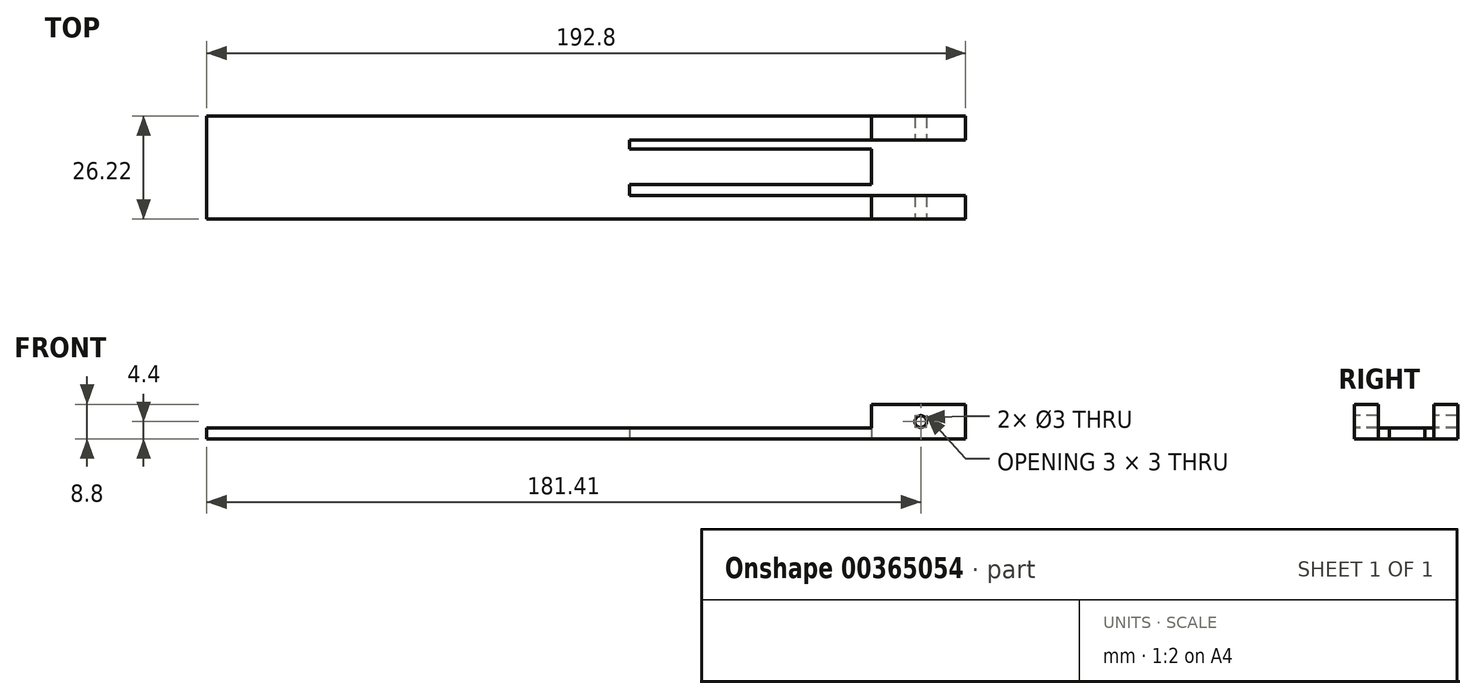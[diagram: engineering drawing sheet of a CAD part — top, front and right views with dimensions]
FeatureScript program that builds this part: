
annotation { "Feature Type Name" : "Feature", "Feature Type Description" : "" }
export const myFeature = defineFeature(function(context is Context, id is Id, definition is map)
    precondition{}
    {
        {
            var Q0;
            Q0=qCreatedBy(makeId("Top.planeOp"),FACE);
            var sketch = newSketch(context, id + "F0", { "sketchPlane" : qUnion([Q0])});
            skLineSegment(sketch, "E0.bottom", {"start": v(75, -12.39) * mm, "end": v(-75, -12.39) * mm});
            skLineSegment(sketch, "E0.top", {"start": v(75, 12.39) * mm, "end": v(-75, 12.39) * mm});
            skLineSegment(sketch, "E0.left", {"start": v(75, -12.39) * mm, "end": v(75, 12.39) * mm});
            skLineSegment(sketch, "E0.right", {"start": v(-75, -12.39) * mm, "end": v(-75, 12.39) * mm});
            skPoint(sketch, "E0.middle", {"position": v(0, 0) * mm});
            skLineSegment(sketch, "E1.bottom", {"start": v(-10.37, 7.78) * mm, "end": v(75, 7.78) * mm});
            skLineSegment(sketch, "E1.top", {"start": v(-10.37, 5.43) * mm, "end": v(75, 5.43) * mm});
            skLineSegment(sketch, "E1.left", {"start": v(-10.37, 7.78) * mm, "end": v(-10.37, 5.43) * mm});
            skLineSegment(sketch, "E2.bottom", {"start": v(-10.37, -3.6) * mm, "end": v(75, -3.6) * mm});
            skLineSegment(sketch, "E2.top", {"start": v(-10.37, -6.34) * mm, "end": v(75, -6.34) * mm});
            skLineSegment(sketch, "E2.left", {"start": v(-10.37, -3.6) * mm, "end": v(-10.37, -6.34) * mm});
            skLineSegment(sketch, "E2.right", {"start": v(75, -3.6) * mm, "end": v(75, -6.34) * mm});
            skSolve(sketch);
        }
        {
            var Q0;
            {var subQ5=sQuery(id+"F0.wireOp",EDGE,"E0.bottom");Q0=makeQuery(id+"F0.imprint","IMPRINT",FACE,{"disambiguationData":[TD([[makeQuery(id+"F0.imprint","IMPRINT",EDGE,{"derivedFrom":subQ5}),-1.0]])]});}
            extrude(context, id + "F1", {"entities" : qUnion([Q0]), "depth" : 2.8 * mm});
        }
        {
            var Q0;
            Q0=makeQuery(id+"F1.opExtrude","SWEPT_FACE",FACE,{"disambiguationData":[OSD([sQuery(id+"F0.wireOp",EDGE,"E0.right")])]});
            extrude(context, id + "F2", {"entities" : qUnion([Q0]), "operationType" : NewBodyOperationType.ADD, "depth" : 42.8 * mm});
        }
        {
            var Q0;
            {var subQ0=sQuery(id+"F0.wireOp",EDGE,"E0.top");Q0=makeQuery(id+"F2.boolean.opBoolean","MERGE",FACE,{"derivedFrom":[makeQuery(id+"F1.opExtrude","SWEPT_FACE",FACE,{"disambiguationData":[OSD([subQ0])]}),makeQuery(id+"F2.opExtrude","SWEPT_FACE",FACE,{"disambiguationData":[OSD([subQ0,sQuery(id+"F0.wireOp",EDGE,"E0.right")])]})]});}
            extrude(context, id + "F3", {"entities" : qUnion([Q0]), "operationType" : NewBodyOperationType.ADD, "depth" : 1.44 * mm});
        }
        {
            var Q0;
            Q0=makeQuery(id+"F3.opExtrude","CAP_FACE",FACE,{"disambiguationData":[OSD([sQuery(id+"F0.wireOp",EDGE,"E0.top"),sQuery(id+"F0.wireOp",EDGE,"E0.right")])],"isStart":false});
            extrude(context, id + "F4", {"entities" : qUnion([Q0]), "operationType" : NewBodyOperationType.REMOVE, "depth" : 85.38 * mm});
        }
        {
            var Q0;
            {var subQ0=sQuery(id+"F0.wireOp",EDGE,"E0.right");var subQ1=sQuery(id+"F0.wireOp",EDGE,"E0.top");Q0=makeQuery(id+"F3.boolean.opBoolean","MERGE",FACE,{"derivedFrom":[makeQuery(id+"F2.boolean.opBoolean","MERGE",FACE,{"derivedFrom":[makeQuery(id+"F1.opExtrude","CAP_FACE",FACE,{"disambiguationData":[OSD([sQuery(id+"F0.wireOp",EDGE,"E0.bottom"),subQ1,sQuery(id+"F0.wireOp",EDGE,"E0.left"),subQ0,sQuery(id+"F0.wireOp",EDGE,"E1.bottom"),sQuery(id+"F0.wireOp",EDGE,"E1.top"),sQuery(id+"F0.wireOp",EDGE,"E1.left"),sQuery(id+"F0.wireOp",EDGE,"E2.bottom"),sQuery(id+"F0.wireOp",EDGE,"E2.top"),sQuery(id+"F0.wireOp",EDGE,"E2.left")])],"isStart":false}),makeQuery(id+"F2.opExtrude","SWEPT_FACE",FACE,{"disambiguationData":[OSD([subQ0]),TDD([makeQuery(id+"F1.opExtrude","CAP_EDGE",EDGE,{"disambiguationData":[OSD([subQ0])],"isStart":false})])]})]}),makeQuery(id+"F3.opExtrude","SWEPT_FACE",FACE,{"disambiguationData":[OSD([subQ1,subQ0]),TDD([makeQuery(id+"F2.boolean.opBoolean","MERGE",EDGE,{"derivedFrom":[makeQuery(id+"F1.opExtrude","CAP_EDGE",EDGE,{"disambiguationData":[OSD([subQ1])],"isStart":false}),makeQuery(id+"F2.opExtrude","SWEPT_EDGE",EDGE,{"disambiguationData":[OSD([subQ1,subQ0]),TDD([makeQuery(id+"F1.opExtrude","CAP_VERTEX",VERTEX,{"disambiguationData":[OSD([subQ1,subQ0])],"isStart":false})])]})]})])]})]});}
            var sketch = newSketch(context, id + "F5", { "sketchPlane" : qUnion([Q0])});
            skLineSegment(sketch, "E3", {"start": v(51.11, 13.83) * mm, "end": v(51.11, 7.78) * mm});
            skLineSegment(sketch, "E4", {"start": v(51.11, -6.34) * mm, "end": v(51.11, -12.39) * mm});
            skSolve(sketch);
        }
        {
            var Q0;
            {var subQ0=sQuery(id+"F5.wireOp",EDGE,"E3");Q0=makeQuery(id+"F5.imprint","IMPRINT",FACE,{"disambiguationData":[TD([[makeQuery(id+"F5.imprint","IMPRINT",EDGE,{"derivedFrom":subQ0}),1.0]])]});}
            var Q1;
            {var subQ0=sQuery(id+"F5.wireOp",EDGE,"E4");Q1=makeQuery(id+"F5.imprint","IMPRINT",FACE,{"disambiguationData":[TD([[makeQuery(id+"F5.imprint","IMPRINT",EDGE,{"derivedFrom":subQ0}),1.0]])]});}
            extrude(context, id + "F6", {"entities" : qUnion([Q0, Q1]), "operationType" : NewBodyOperationType.ADD, "depth" : 6 * mm});
        }
        {
            var Q0;
            {var subQ0=sQuery(id+"F0.wireOp",EDGE,"E0.right");var subQ1=sQuery(id+"F0.wireOp",EDGE,"E0.bottom");Q0=makeQuery(id+"F6.boolean.opBoolean","MERGE",FACE,{"derivedFrom":[makeQuery(id+"F2.boolean.opBoolean","MERGE",FACE,{"derivedFrom":[makeQuery(id+"F1.opExtrude","SWEPT_FACE",FACE,{"disambiguationData":[OSD([subQ1])]}),makeQuery(id+"F2.opExtrude","SWEPT_FACE",FACE,{"disambiguationData":[OSD([subQ1,subQ0])]})]}),makeQuery(id+"F6.opExtrude","SWEPT_FACE",FACE,{"disambiguationData":[OSD([subQ1,subQ0])]})]});}
            var sketch = newSketch(context, id + "F7", { "sketchPlane" : qUnion([Q0])});
            skCircle(sketch, "E5", {"center": v(63.6, 4.4) * mm, "radius": 1.5 * mm});
            skPoint(sketch, "E5.centerSnap0", {"position": v(75, 4.4) * mm});
            skSolve(sketch);
        }
        {
            var Q0;
            Q0 = qSketchRegion(id + "F7", true);
            extrude(context, id + "F8", {"entities" : qUnion([Q0]), "operationType" : NewBodyOperationType.REMOVE, "oppositeDirection" : true, "depth" : 27.5 * mm});
        }
        {
            var Q0;
            {var subQ0=sQuery(id+"F0.wireOp",EDGE,"E0.left");Q0=makeQuery(id+"F1.opExtrude","SWEPT_FACE",FACE,{"disambiguationData":[OSD([subQ0]),TDD([makeQuery(id+"F0.imprint","IMPRINT",EDGE,{"disambiguationData":[TD([[makeQuery(id+"F0.imprint","INTERSECT",VERTEX,{"derivedFrom":[subQ0,sQuery(id+"F0.wireOp",EDGE,"E1.top")]}),1.0]])],"derivedFrom":subQ0})])]});}
            extrude(context, id + "F9", {"entities" : qUnion([Q0]), "operationType" : NewBodyOperationType.REMOVE, "oppositeDirection" : true, "depth" : 23.9 * mm});
        }
    });
